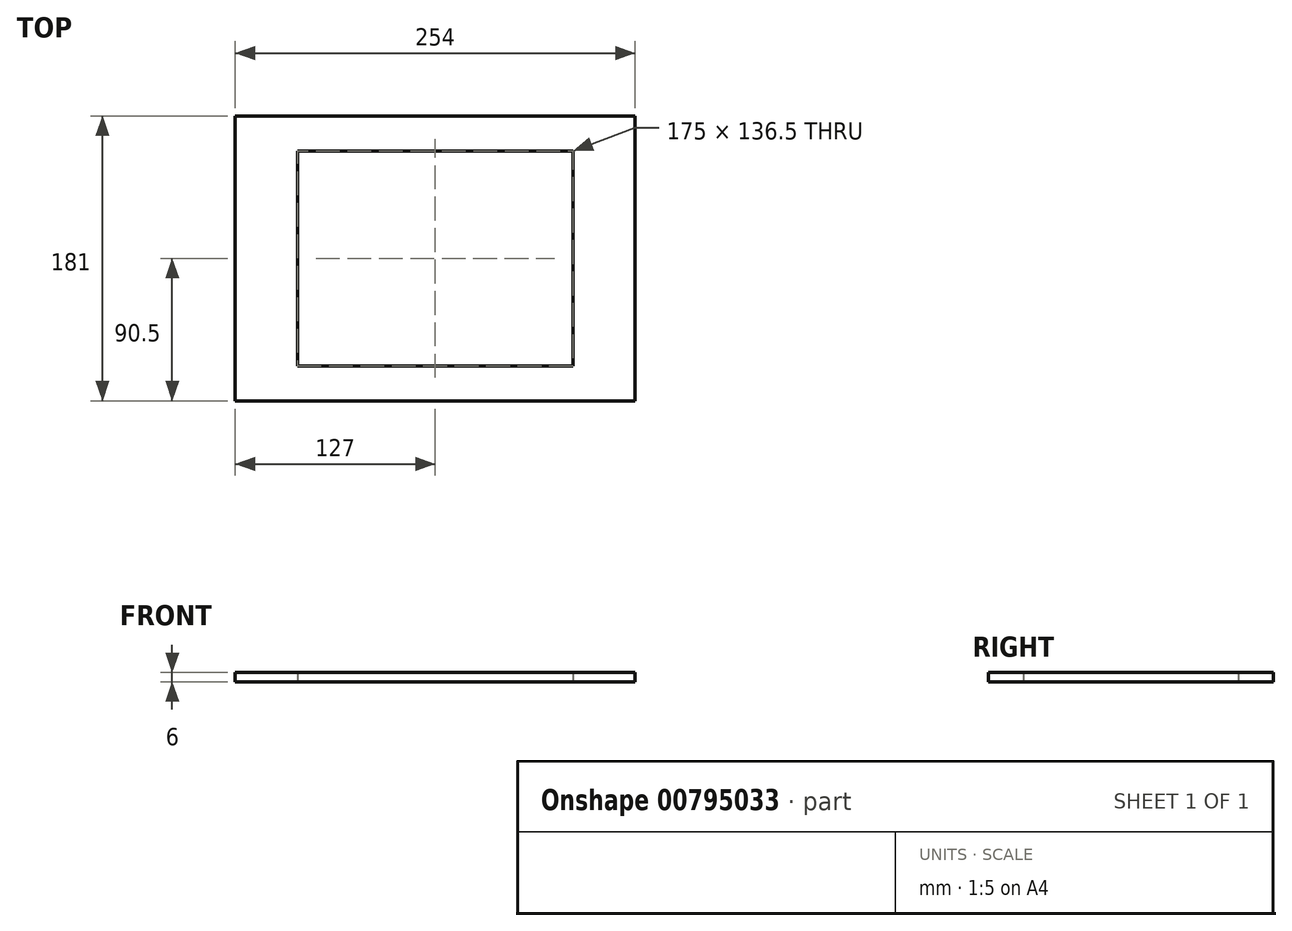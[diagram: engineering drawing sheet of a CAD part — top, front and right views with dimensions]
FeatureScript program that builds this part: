
annotation { "Feature Type Name" : "Feature", "Feature Type Description" : "" }
export const myFeature = defineFeature(function(context is Context, id is Id, definition is map)
    precondition{}
    {
        {
            var Q0;
            Q0=qCreatedBy(makeId("Top.planeOp"),FACE);
            var sketch = newSketch(context, id + "F0", { "sketchPlane" : qUnion([Q0])});
            skLineSegment(sketch, "E0.bottom", {"start": v(127, 90.5) * mm, "end": v(-127, 90.5) * mm});
            skLineSegment(sketch, "E0.top", {"start": v(127, -90.5) * mm, "end": v(-127, -90.5) * mm});
            skLineSegment(sketch, "E0.left", {"start": v(127, 90.5) * mm, "end": v(127, -90.5) * mm});
            skLineSegment(sketch, "E0.right", {"start": v(-127, 90.5) * mm, "end": v(-127, -90.5) * mm});
            skPoint(sketch, "E0.middle", {"position": v(0, 0) * mm});
            skLineSegment(sketch, "E1.bottom", {"start": v(-87.5, 68.25) * mm, "end": v(87.5, 68.25) * mm});
            skLineSegment(sketch, "E1.top", {"start": v(-87.5, -68.25) * mm, "end": v(87.5, -68.25) * mm});
            skLineSegment(sketch, "E1.left", {"start": v(-87.5, 68.25) * mm, "end": v(-87.5, -68.25) * mm});
            skLineSegment(sketch, "E1.right", {"start": v(87.5, 68.25) * mm, "end": v(87.5, -68.25) * mm});
            skSolve(sketch);
        }
        {
            var Q0;
            Q0=makeQuery(id+"F0.imprint","IMPRINT",FACE,{"disambiguationData":[TD([[makeQuery(id+"F0.imprint","IMPRINT",EDGE,{"derivedFrom":sQuery(id+"F0.wireOp",EDGE,"E0.bottom")}),1.0]])]});
            extrude(context, id + "F1", {"entities" : qUnion([Q0]), "depth" : 6 * mm, "offsetDistance" : 25 * mm});
        }
    });
